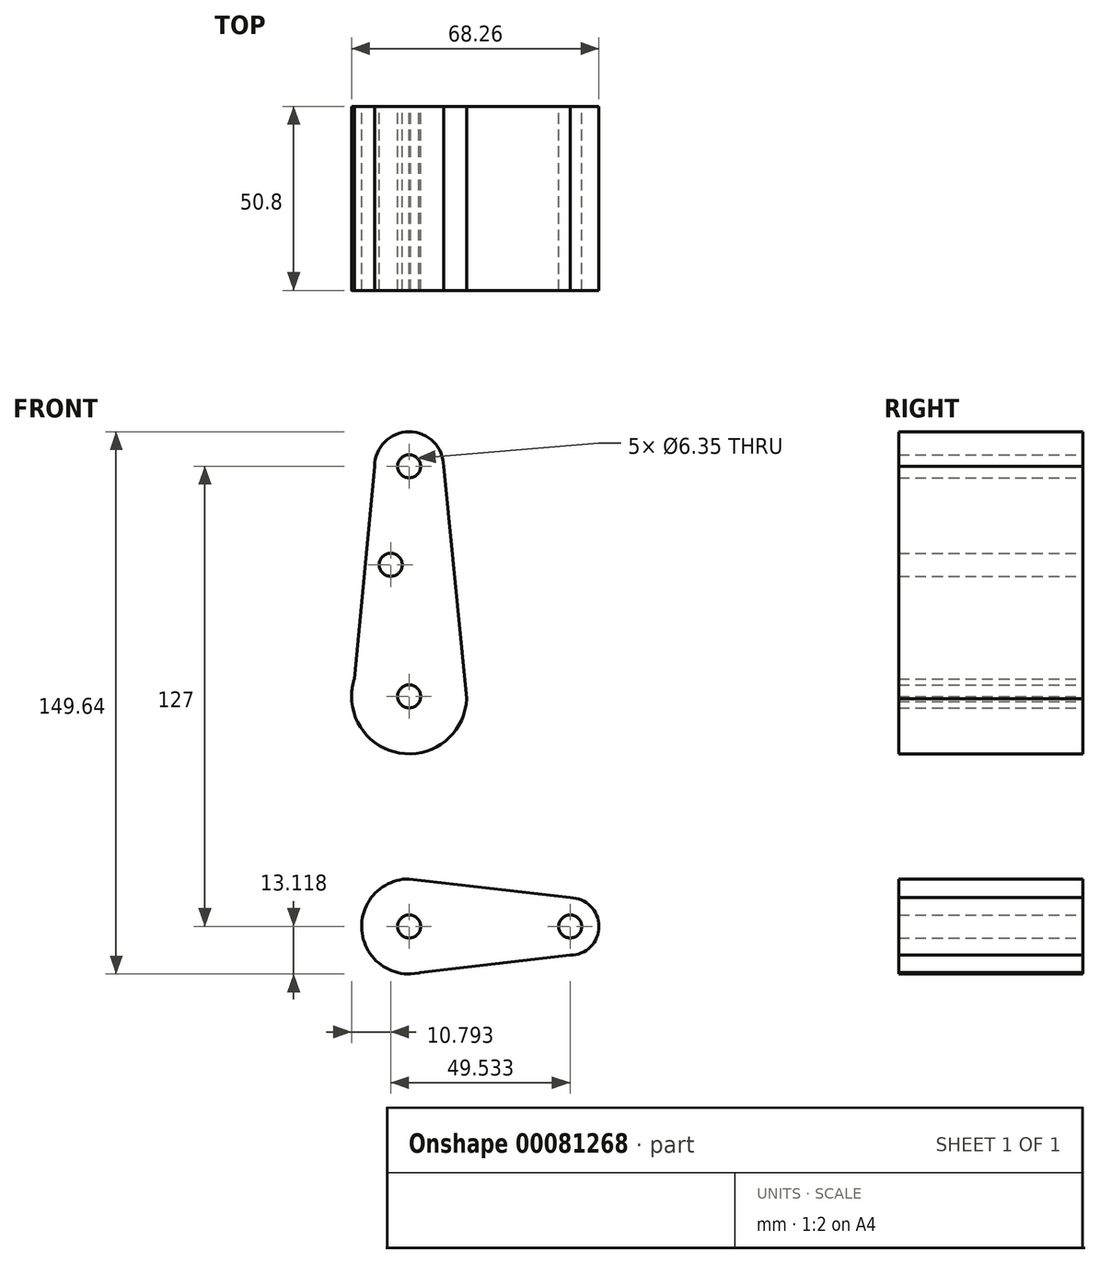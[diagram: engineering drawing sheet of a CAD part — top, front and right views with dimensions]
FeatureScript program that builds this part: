
annotation { "Feature Type Name" : "Feature", "Feature Type Description" : "" }
export const myFeature = defineFeature(function(context is Context, id is Id, definition is map)
    precondition{}
    {
        {
            var Q0;
            Q0=qCreatedBy(makeId("Front.planeOp"),FACE);
            var sketch = newSketch(context, id + "F0", { "sketchPlane" : qUnion([Q0])});
            skLineSegment(sketch, "E0", {"start": v(0, 0) * mm, "end": v(0, 0) * mm});
            skLineSegment(sketch, "E1", {"start": v(-83.02, 96.95) * mm, "end": v(-83.02, -30.05) * mm, "construction": true});
            skLineSegment(sketch, "E2", {"start": v(-83.02, -30.05) * mm, "end": v(-38.57, -30.05) * mm, "construction": true});
            skCircle(sketch, "E3", {"center": v(-83.02, -30.05) * mm, "radius": 13.11 * mm});
            skCircle(sketch, "E4", {"center": v(-83.02, 96.95) * mm, "radius": 9.53 * mm});
            skCircle(sketch, "E5", {"center": v(-38.57, -30.05) * mm, "radius": 7.94 * mm});
            skCircle(sketch, "E6", {"center": v(-83.02, 33.45) * mm, "radius": 15.88 * mm});
            skLineSegment(sketch, "E7", {"start": v(-82.66, -43.16) * mm, "end": v(-38.57, -37.99) * mm});
            skLineSegment(sketch, "E8", {"start": v(-38.57, -37.99) * mm, "end": v(-83.02, -43.16) * mm});
            skLineSegment(sketch, "E9", {"start": v(-83.02, -16.94) * mm, "end": v(-38.57, -22.11) * mm});
            skLineSegment(sketch, "E10", {"start": v(-83.02, 33.45) * mm, "end": v(-120.07, 33.45) * mm});
            skLineSegment(sketch, "E11", {"start": v(-83.02, -30.05) * mm, "end": v(-120.07, -30.05) * mm});
            skLineSegment(sketch, "E12", {"start": v(-120.07, -30.05) * mm, "end": v(-136.52, -30.05) * mm});
            skLineSegment(sketch, "E13", {"start": v(-83.02, 96.95) * mm, "end": v(-136.52, 96.95) * mm});
            skLineSegment(sketch, "E14", {"start": v(-69.9, -30.05) * mm, "end": v(-67.16, 32.75) * mm});
            skLineSegment(sketch, "E15", {"start": v(-98.9, 33.45) * mm, "end": v(-96.15, -30.05) * mm});
            skCircle(sketch, "E16", {"center": v(-83.02, 96.95) * mm, "radius": 3.18 * mm});
            skCircle(sketch, "E17", {"center": v(-83.02, 33.45) * mm, "radius": 3.18 * mm});
            skCircle(sketch, "E18", {"center": v(-83.02, -30.05) * mm, "radius": 3.18 * mm});
            skCircle(sketch, "E19", {"center": v(-38.57, -30.05) * mm, "radius": 3.18 * mm});
            skCircle(sketch, "E20", {"center": v(-88.1, 69.77) * mm, "radius": 3.18 * mm});
            skLineSegment(sketch, "E21", {"start": v(-88.1, 69.77) * mm, "end": v(0, 69.77) * mm});
            skLineSegment(sketch, "E22", {"start": v(-83.02, 33.45) * mm, "end": v(0, 33.45) * mm});
            skLineSegment(sketch, "E23", {"start": v(-92.55, 96.95) * mm, "end": v(-98.14, 38.31) * mm});
            skLineSegment(sketch, "E24", {"start": v(-73.5, 96.95) * mm, "end": v(-67.16, 32.75) * mm});
            skSolve(sketch);
        }
        {
            var Q0;
            Q0=makeQuery(id+"F0.imprint","IMPRINT",FACE,{"disambiguationData":[TD([[makeQuery(id+"F0.imprint","IMPRINT",EDGE,{"derivedFrom":sQuery(id+"F0.wireOp",EDGE,"E20")}),-1.0]])]});
            var Q1;
            {var subQ0=sQuery(id+"F0.wireOp",EDGE,"E17");var subQ1=sQuery(id+"F0.wireOp",EDGE,"E10");var subQ2=makeQuery(id+"F0.imprint","INTERSECT",VERTEX,{"derivedFrom":[subQ1,subQ0]});Q1=makeQuery(id+"F0.imprint","IMPRINT",FACE,{"disambiguationData":[TD([[makeQuery(id+"F0.imprint","IMPRINT",EDGE,{"disambiguationData":[TD([[subQ2,-1.0]])],"derivedFrom":subQ0}),-1.0]])]});}
            var Q2;
            {var subQ5=sQuery(id+"F0.wireOp",EDGE,"E6");var subQ7=makeQuery(id+"F0.imprint","INTERSECT",VERTEX,{"derivedFrom":[subQ5,sQuery(id+"F0.wireOp",EDGE,"E23")]});Q2=makeQuery(id+"F0.imprint","IMPRINT",FACE,{"disambiguationData":[TD([[makeQuery(id+"F0.imprint","IMPRINT",EDGE,{"disambiguationData":[TD([[subQ7,1.0]])],"derivedFrom":subQ5}),1.0]])]});}
            var Q3;
            {var subQ1=sQuery(id+"F0.wireOp",EDGE,"E9");var subQ3=sQuery(id+"F0.wireOp",EDGE,"E3");var subQ5=makeQuery(id+"F0.imprint","INTERSECT",VERTEX,{"disambiguationData":[OD(0.0)],"derivedFrom":[subQ3,subQ1]});Q3=makeQuery(id+"F0.imprint","IMPRINT",FACE,{"disambiguationData":[TD([[makeQuery(id+"F0.imprint","IMPRINT",EDGE,{"disambiguationData":[TD([[subQ5,1.0]])],"derivedFrom":subQ3}),-1.0]])]});}
            var Q4;
            Q4=makeQuery(id+"F0.imprint","IMPRINT",FACE,{"disambiguationData":[TD([[makeQuery(id+"F0.imprint","IMPRINT",EDGE,{"derivedFrom":sQuery(id+"F0.wireOp",EDGE,"E16")}),-1.0]])]});
            var Q5;
            Q5=makeQuery(id+"F0.imprint","IMPRINT",FACE,{"disambiguationData":[TD([[makeQuery(id+"F0.imprint","IMPRINT",EDGE,{"derivedFrom":sQuery(id+"F0.wireOp",EDGE,"E18")}),-1.0]])]});
            var Q6;
            {var subQ5=sQuery(id+"F0.wireOp",EDGE,"E14");var subQ7=sQuery(id+"F0.wireOp",EDGE,"E3");var subQ9=makeQuery(id+"F0.imprint","INTERSECT",VERTEX,{"derivedFrom":[subQ7,subQ5]});Q6=makeQuery(id+"F0.imprint","IMPRINT",FACE,{"disambiguationData":[TD([[makeQuery(id+"F0.imprint","IMPRINT",EDGE,{"disambiguationData":[TD([[subQ9,1.0]])],"derivedFrom":subQ7}),-1.0]])]});}
            var Q7;
            Q7=makeQuery(id+"F0.imprint","IMPRINT",FACE,{"disambiguationData":[TD([[makeQuery(id+"F0.imprint","IMPRINT",EDGE,{"derivedFrom":sQuery(id+"F0.wireOp",EDGE,"E19")}),-1.0]])]});
            var Q8;
            {var subQ0=sQuery(id+"F0.wireOp",EDGE,"E14");var subQ1=sQuery(id+"F0.wireOp",EDGE,"E3");var subQ2=makeQuery(id+"F0.imprint","INTERSECT",VERTEX,{"derivedFrom":[subQ1,subQ0]});Q8=makeQuery(id+"F0.imprint","IMPRINT",FACE,{"disambiguationData":[TD([[makeQuery(id+"F0.imprint","IMPRINT",EDGE,{"disambiguationData":[TD([[subQ2,-1.0]])],"derivedFrom":subQ1}),-1.0]])]});}
            extrude(context, id + "F1", {"entities" : qUnion([Q0, Q1, Q2, Q3, Q4, Q5, Q6, Q7, Q8]), "endBound" : BoundingType.SYMMETRIC, "depth" : 50.8 * mm});
        }
    });
